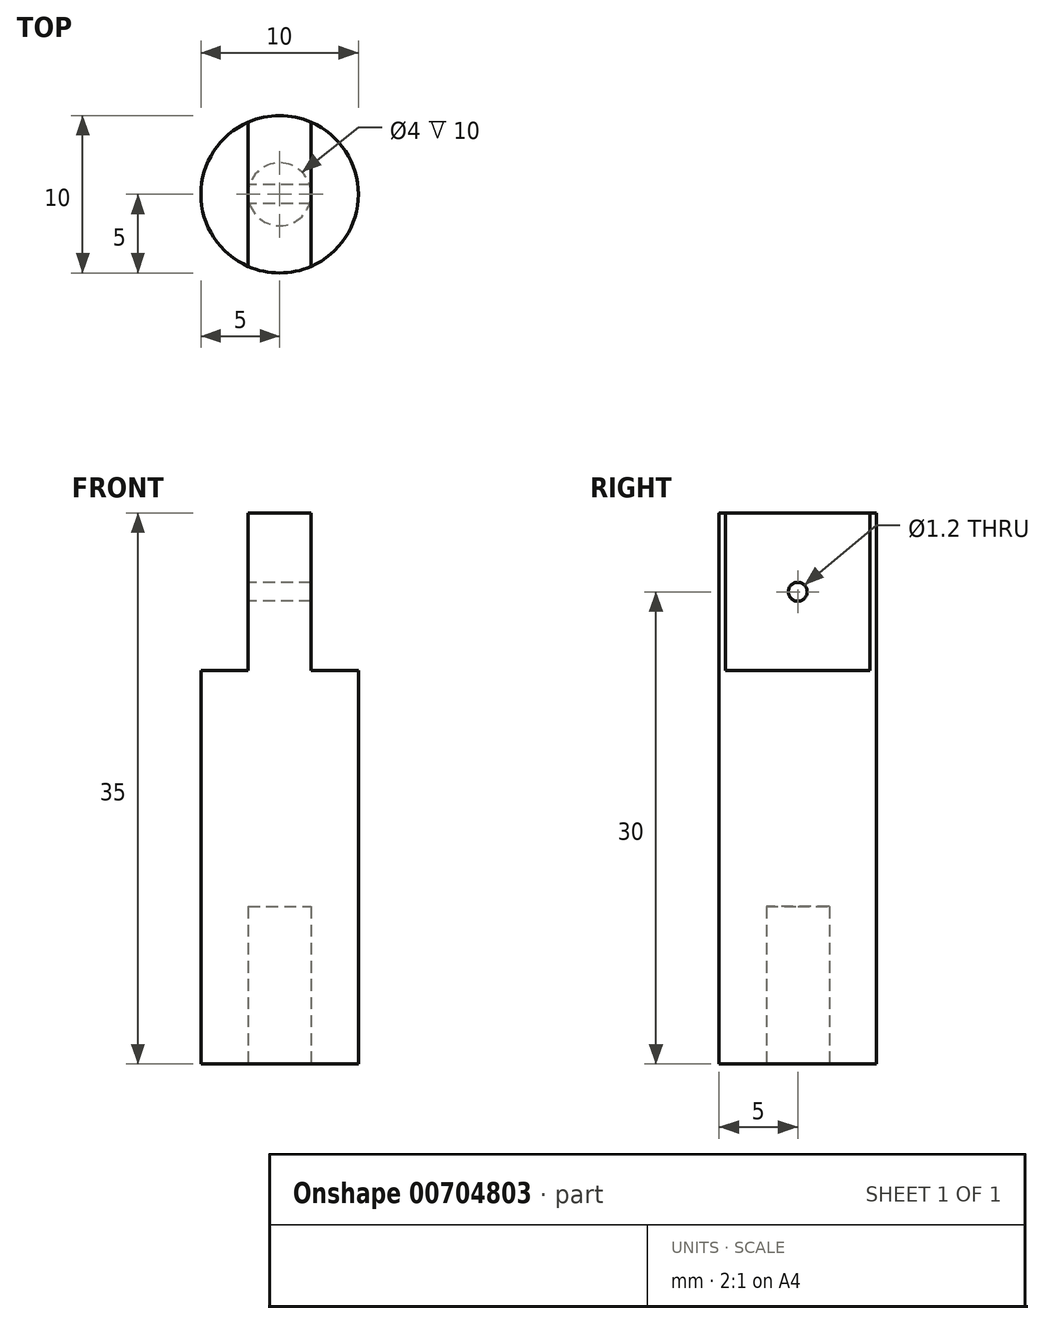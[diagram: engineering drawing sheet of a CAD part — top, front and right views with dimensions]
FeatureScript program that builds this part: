
annotation { "Feature Type Name" : "Feature", "Feature Type Description" : "" }
export const myFeature = defineFeature(function(context is Context, id is Id, definition is map)
    precondition{}
    {
        {
            var Q0;
            Q0=qCreatedBy(makeId("Top.planeOp"),FACE);
            var sketch = newSketch(context, id + "F0", { "sketchPlane" : qUnion([Q0])});
            skCircle(sketch, "E0", {"center": v(0, 0) * mm, "radius": 5 * mm});
            skSolve(sketch);
        }
        {
            var Q0;
            Q0=makeQuery(id+"F0.imprint","IMPRINT",FACE,{"disambiguationData":[TD([[makeQuery(id+"F0.imprint","IMPRINT",EDGE,{"derivedFrom":sQuery(id+"F0.wireOp",EDGE,"E0")}),1.0]])]});
            extrude(context, id + "F1", {"entities" : qUnion([Q0]), "depth" : 25 * mm, "offsetDistance" : 25 * mm});
        }
        {
            var Q0;
            Q0=makeQuery(id+"F1.opExtrude","CAP_FACE",FACE,{"disambiguationData":[OSD([sQuery(id+"F0.wireOp",EDGE,"E0")])],"isStart":true});
            var sketch = newSketch(context, id + "F2", { "sketchPlane" : qUnion([Q0])});
            skCircle(sketch, "E1", {"center": v(0, 0) * mm, "radius": 2 * mm});
            skSolve(sketch);
        }
        {
            var Q0;
            Q0=makeQuery(id+"F2.imprint","IMPRINT",FACE,{"disambiguationData":[TD([[makeQuery(id+"F2.imprint","IMPRINT",EDGE,{"derivedFrom":sQuery(id+"F2.wireOp",EDGE,"E1")}),1.0]])]});
            extrude(context, id + "F3", {"entities" : qUnion([Q0]), "operationType" : NewBodyOperationType.REMOVE, "oppositeDirection" : true, "depth" : 10 * mm, "offsetDistance" : 25 * mm});
        }
        {
            var Q0;
            Q0=makeQuery(id+"F1.opExtrude","CAP_FACE",FACE,{"disambiguationData":[OSD([sQuery(id+"F0.wireOp",EDGE,"E0")])],"isStart":false});
            var sketch = newSketch(context, id + "F4", { "sketchPlane" : qUnion([Q0])});
            skLineSegment(sketch, "E2", {"start": v(0, 5) * mm, "end": v(-2, 5) * mm});
            skLineSegment(sketch, "E3", {"start": v(-2, 5) * mm, "end": v(-2, -5) * mm});
            skLineSegment(sketch, "E4", {"start": v(-2, -5) * mm, "end": v(0, -5) * mm});
            skLineSegment(sketch, "E5", {"start": v(0, -5) * mm, "end": v(2, -5) * mm});
            skLineSegment(sketch, "E6", {"start": v(2, -5) * mm, "end": v(2, 5) * mm});
            skLineSegment(sketch, "E7", {"start": v(2, 5) * mm, "end": v(0, 5) * mm});
            skSolve(sketch);
        }
        {
            var Q0;
            {var subQ0=makeQuery(id+"F1.opExtrude","CAP_EDGE",EDGE,{"disambiguationData":[OSD([sQuery(id+"F0.wireOp",EDGE,"E0")])],"isStart":false});var subQ4=sQuery(id+"F4.wireOp",EDGE,"E3");var subQ5=makeQuery(id+"F4.imprint","INTERSECT",VERTEX,{"disambiguationData":[OD(0.0)],"derivedFrom":[subQ0,subQ4]});Q0=makeQuery(id+"F4.imprint","IMPRINT",FACE,{"disambiguationData":[TD([[makeQuery(id+"F4.imprint","IMPRINT",EDGE,{"disambiguationData":[TD([[subQ5,-1.0]])],"derivedFrom":subQ4}),1.0]])]});}
            extrude(context, id + "F5", {"entities" : qUnion([Q0]), "operationType" : NewBodyOperationType.ADD, "depth" : 10 * mm, "offsetDistance" : 25 * mm});
        }
        {
            var Q0;
            Q0=makeQuery(id+"F5.opExtrude","SWEPT_FACE",FACE,{"disambiguationData":[OSD([sQuery(id+"F4.wireOp",EDGE,"E3")])]});
            var sketch = newSketch(context, id + "F6", { "sketchPlane" : qUnion([Q0])});
            skCircle(sketch, "E8", {"center": v(0, 30) * mm, "radius": 2 * mm});
            skPoint(sketch, "E8.centerSnap0", {"position": v(-4.58, 30) * mm});
            skSolve(sketch);
        }
        {
            var Q0;
            Q0=sQuery(id+"F6.wireOp",VERTEX,"E8.center");
            var Q1;
            Q1=makeQuery(id+"F1.opExtrude","SWEPT_BODY",BODY,{"disambiguationData":[OSD([sQuery(id+"F0.wireOp",EDGE,"E0")])]});
            hole(context, id + "F7", {"style" : HoleStyle.SIMPLE, "endStyle" : HoleEndStyle.THROUGH, "holeDiameter" : 1.2 * mm, "majorDiameter" : 5 * mm, "isTappedThrough" : true, "tappedDepth" : 12 * mm, "tapClearance" : 3, "locations" : qUnion([Q0]), "scope" : qUnion([Q1])});
        }
    });
